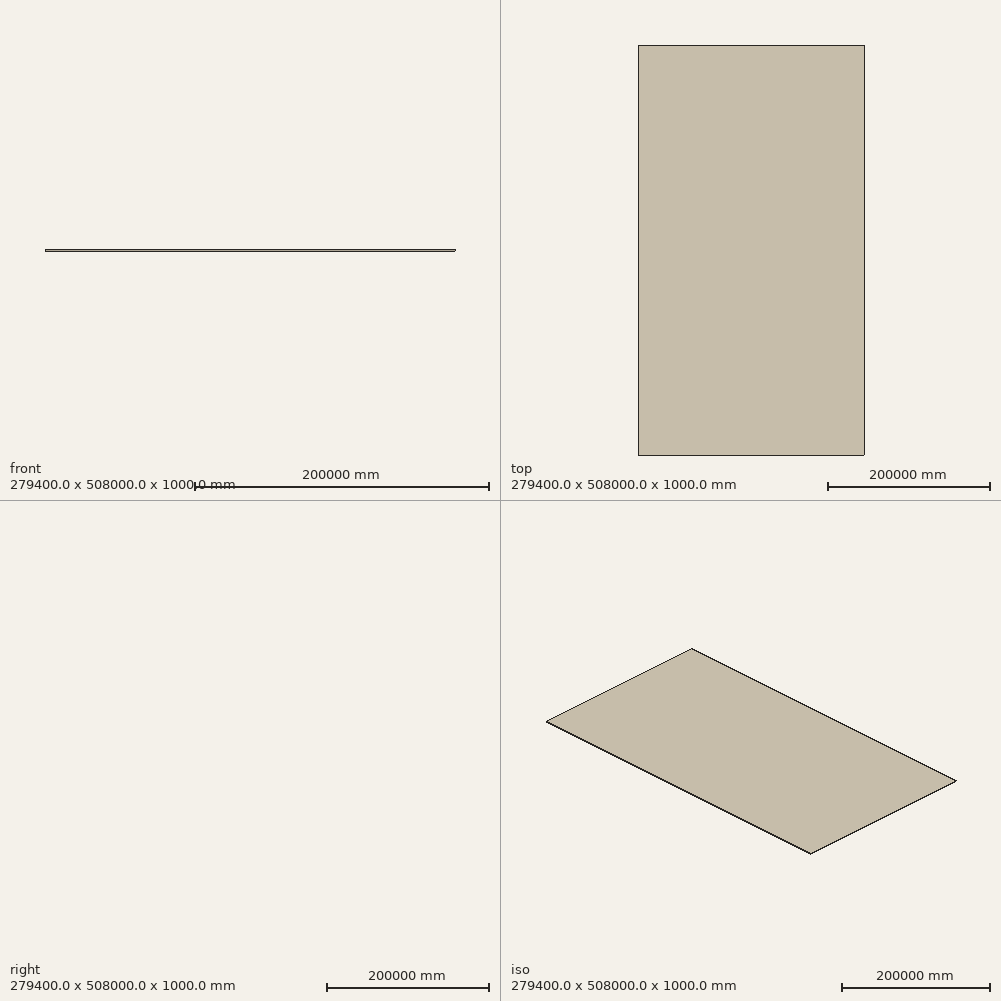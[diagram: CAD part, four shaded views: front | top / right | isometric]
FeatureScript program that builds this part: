
annotation { "Feature Type Name" : "Feature", "Feature Type Description" : "" }
export const myFeature = defineFeature(function(context is Context, id is Id, definition is map)
    precondition{}
    {
        {
            var Q0;
            Q0=qCreatedBy(makeId("Top.planeOp"),FACE);
            var sketch = newSketch(context, id + "F0", { "sketchPlane" : qUnion([Q0])});
            skLineSegment(sketch, "E0.bottom", {"start": v(139700, 254000) * mm, "end": v(-139700, 254000) * mm});
            skLineSegment(sketch, "E0.top", {"start": v(139700, -254000) * mm, "end": v(-139700, -254000) * mm});
            skLineSegment(sketch, "E0.left", {"start": v(139700, 254000) * mm, "end": v(139700, -254000) * mm});
            skLineSegment(sketch, "E0.right", {"start": v(-139700, 254000) * mm, "end": v(-139700, -254000) * mm});
            skPoint(sketch, "E0.middle", {"position": v(0, 0) * mm});
            skSolve(sketch);
        }
        {
            var Q0;
            Q0=makeQuery(id+"F0.imprint","IMPRINT",FACE,{"disambiguationData":[TD([[makeQuery(id+"F0.imprint","IMPRINT",EDGE,{"derivedFrom":sQuery(id+"F0.wireOp",EDGE,"E0.bottom")}),1.0]])]});
            extrude(context, id + "F1", {"entities" : qUnion([Q0]), "depth" : 1000 * mm, "offsetDistance" : 25.4 * mm});
        }
    });
